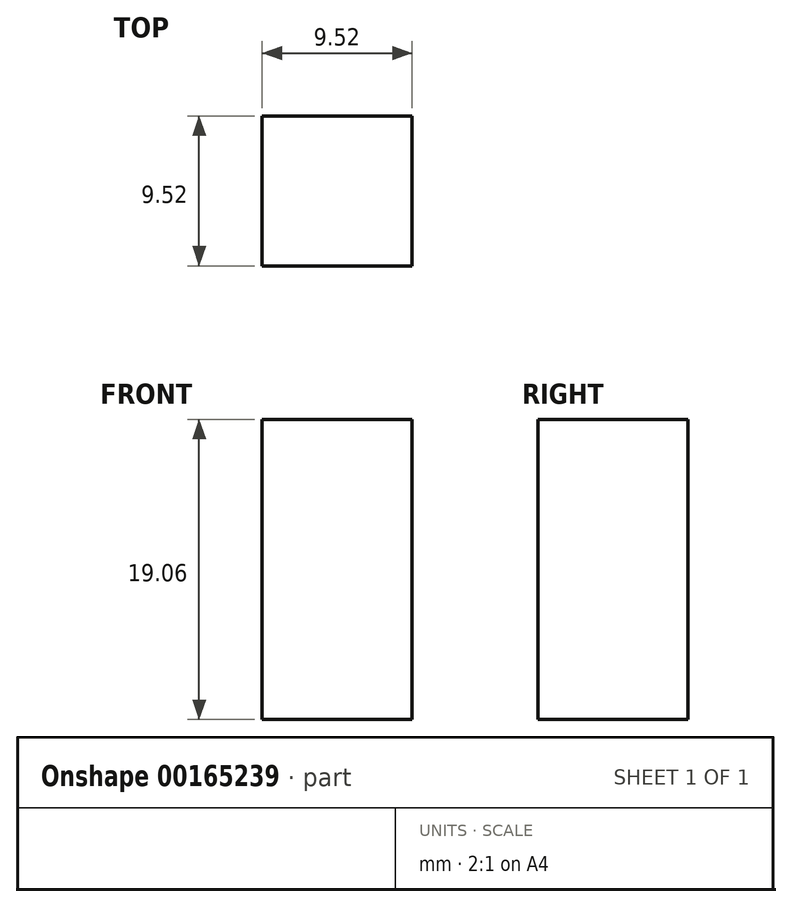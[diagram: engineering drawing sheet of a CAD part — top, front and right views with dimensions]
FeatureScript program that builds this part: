
annotation { "Feature Type Name" : "Feature", "Feature Type Description" : "" }
export const myFeature = defineFeature(function(context is Context, id is Id, definition is map)
    precondition{}
    {
        {
            var Q0;
            Q0=qCreatedBy(makeId("Top.planeOp"),FACE);
            var sketch = newSketch(context, id + "F0", { "sketchPlane" : qUnion([Q0])});
            skLineSegment(sketch, "E0.bottom", {"start": v(4.76, 4.76) * mm, "end": v(-4.76, 4.76) * mm});
            skLineSegment(sketch, "E0.top", {"start": v(4.76, -4.76) * mm, "end": v(-4.76, -4.76) * mm});
            skLineSegment(sketch, "E0.left", {"start": v(4.76, 4.76) * mm, "end": v(4.76, -4.76) * mm});
            skLineSegment(sketch, "E0.right", {"start": v(-4.76, 4.76) * mm, "end": v(-4.76, -4.76) * mm});
            skPoint(sketch, "E0.middle", {"position": v(0, 0) * mm});
            skSolve(sketch);
        }
        {
            var Q0;
            Q0 = qSketchRegion(id + "F0", true);
            extrude(context, id + "F1", {"entities" : qUnion([Q0]), "depth" : 19.06 * mm});
        }
    });
